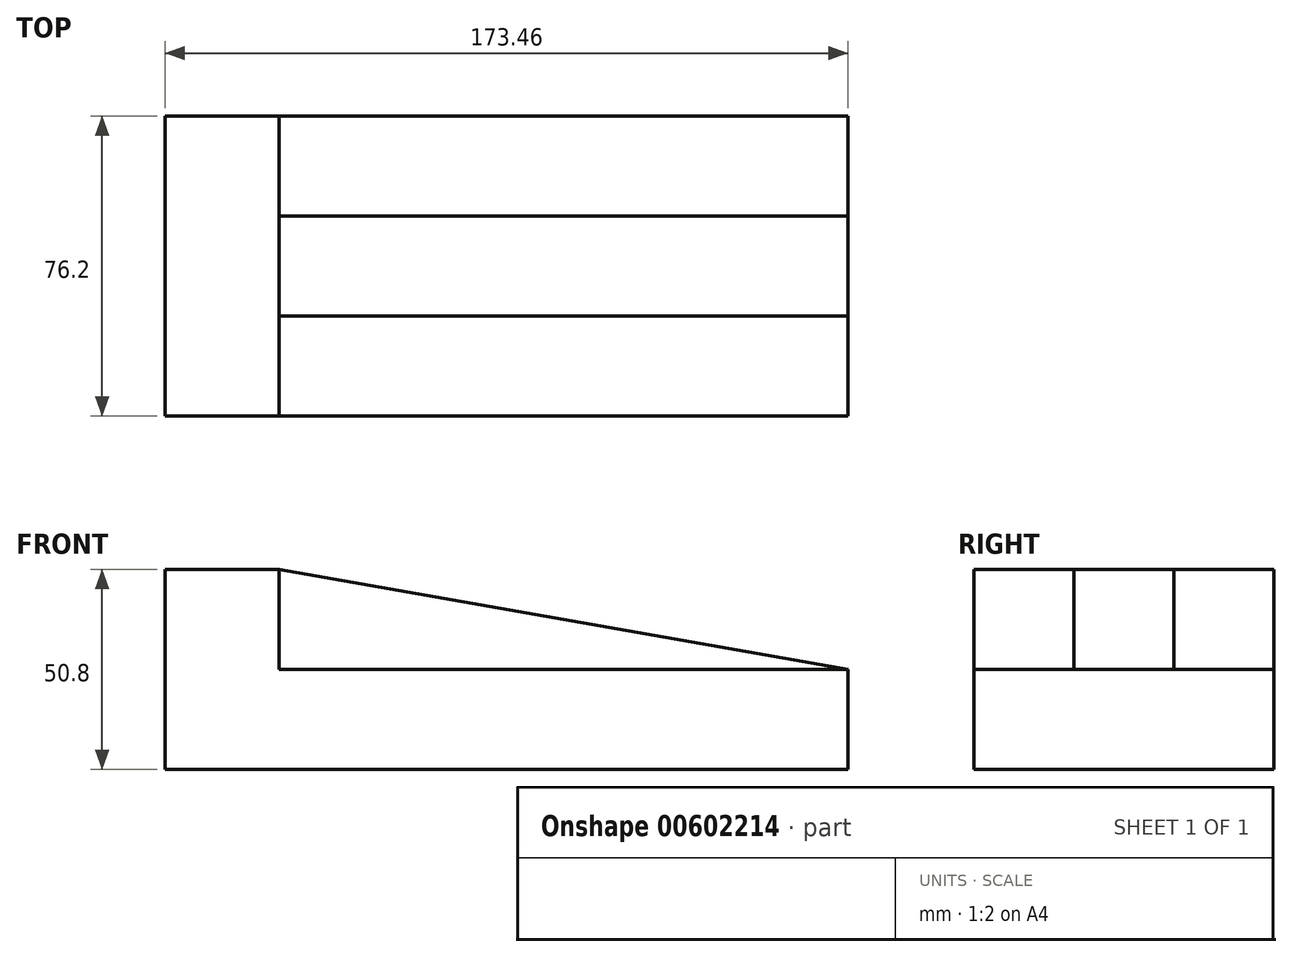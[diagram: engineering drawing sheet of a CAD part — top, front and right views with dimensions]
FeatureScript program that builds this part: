
annotation { "Feature Type Name" : "Feature", "Feature Type Description" : "" }
export const myFeature = defineFeature(function(context is Context, id is Id, definition is map)
    precondition{}
    {
        {
            var Q0;
            Q0=qCreatedBy(makeId("Front.planeOp"),FACE);
            var sketch = newSketch(context, id + "F0", { "sketchPlane" : qUnion([Q0])});
            skLineSegment(sketch, "E0", {"start": v(28.91, 50.8) * mm, "end": v(28.91, 25.4) * mm});
            skLineSegment(sketch, "E1", {"start": v(28.91, 25.4) * mm, "end": v(173.46, 25.4) * mm});
            skLineSegment(sketch, "E2", {"start": v(173.46, 25.4) * mm, "end": v(173.46, 0) * mm});
            skLineSegment(sketch, "E3", {"start": v(173.46, 0) * mm, "end": v(0, 0) * mm});
            skLineSegment(sketch, "E4", {"start": v(0, 0) * mm, "end": v(0, 50.8) * mm});
            skLineSegment(sketch, "E5", {"start": v(0, 50.8) * mm, "end": v(28.91, 50.8) * mm});
            skSolve(sketch);
        }
        {
            var Q0;
            Q0=makeQuery(id+"F0.imprint","IMPRINT",FACE,{"disambiguationData":[TD([[makeQuery(id+"F0.imprint","IMPRINT",EDGE,{"derivedFrom":sQuery(id+"F0.wireOp",EDGE,"E0")}),-1.0]])]});
            extrude(context, id + "F1", {"entities" : qUnion([Q0]), "depth" : 76.2 * mm, "offsetDistance" : 25.4 * mm});
        }
        {
            var Q0;
            Q0=makeQuery(id+"F1.opExtrude","SWEPT_FACE",FACE,{"disambiguationData":[OSD([sQuery(id+"F0.wireOp",EDGE,"E1")])]});
            var sketch = newSketch(context, id + "F2", { "sketchPlane" : qUnion([Q0])});
            skLineSegment(sketch, "E6", {"start": v(28.91, -25.4) * mm, "end": v(173.46, -25.4) * mm});
            skLineSegment(sketch, "E7", {"start": v(173.46, -25.4) * mm, "end": v(173.46, -50.8) * mm});
            skLineSegment(sketch, "E8", {"start": v(173.46, -50.8) * mm, "end": v(28.91, -50.8) * mm});
            skLineSegment(sketch, "E9", {"start": v(28.91, -50.8) * mm, "end": v(28.91, -25.4) * mm});
            skSolve(sketch);
        }
        {
            var Q0;
            Q0=makeQuery(id+"F2.imprint","IMPRINT",FACE,{"disambiguationData":[TD([[makeQuery(id+"F2.imprint","IMPRINT",EDGE,{"derivedFrom":sQuery(id+"F2.wireOp",EDGE,"E6")}),-1.0]])]});
            extrude(context, id + "F3", {"entities" : qUnion([Q0]), "operationType" : NewBodyOperationType.ADD, "depth" : 25.4 * mm, "offsetDistance" : 25.4 * mm});
        }
        {
            var Q0;
            Q0=makeQuery(id+"F3.opExtrude","SWEPT_FACE",FACE,{"disambiguationData":[OSD([sQuery(id+"F2.wireOp",EDGE,"E8")])]});
            var sketch = newSketch(context, id + "F4", { "sketchPlane" : qUnion([Q0])});
            skLineSegment(sketch, "E10", {"start": v(28.91, 50.8) * mm, "end": v(173.46, 25.4) * mm});
            skSolve(sketch);
        }
        {
            var Q0;
            Q0=makeQuery(id+"F4.imprint","IMPRINT",FACE,{"disambiguationData":[TD([[makeQuery(id+"F4.imprint","IMPRINT",EDGE,{"derivedFrom":sQuery(id+"F4.wireOp",EDGE,"E10")}),1.0]])]});
            extrude(context, id + "F5", {"entities" : qUnion([Q0]), "operationType" : NewBodyOperationType.REMOVE, "oppositeDirection" : true, "depth" : 25.4 * mm, "offsetDistance" : 25.4 * mm});
        }
    });
